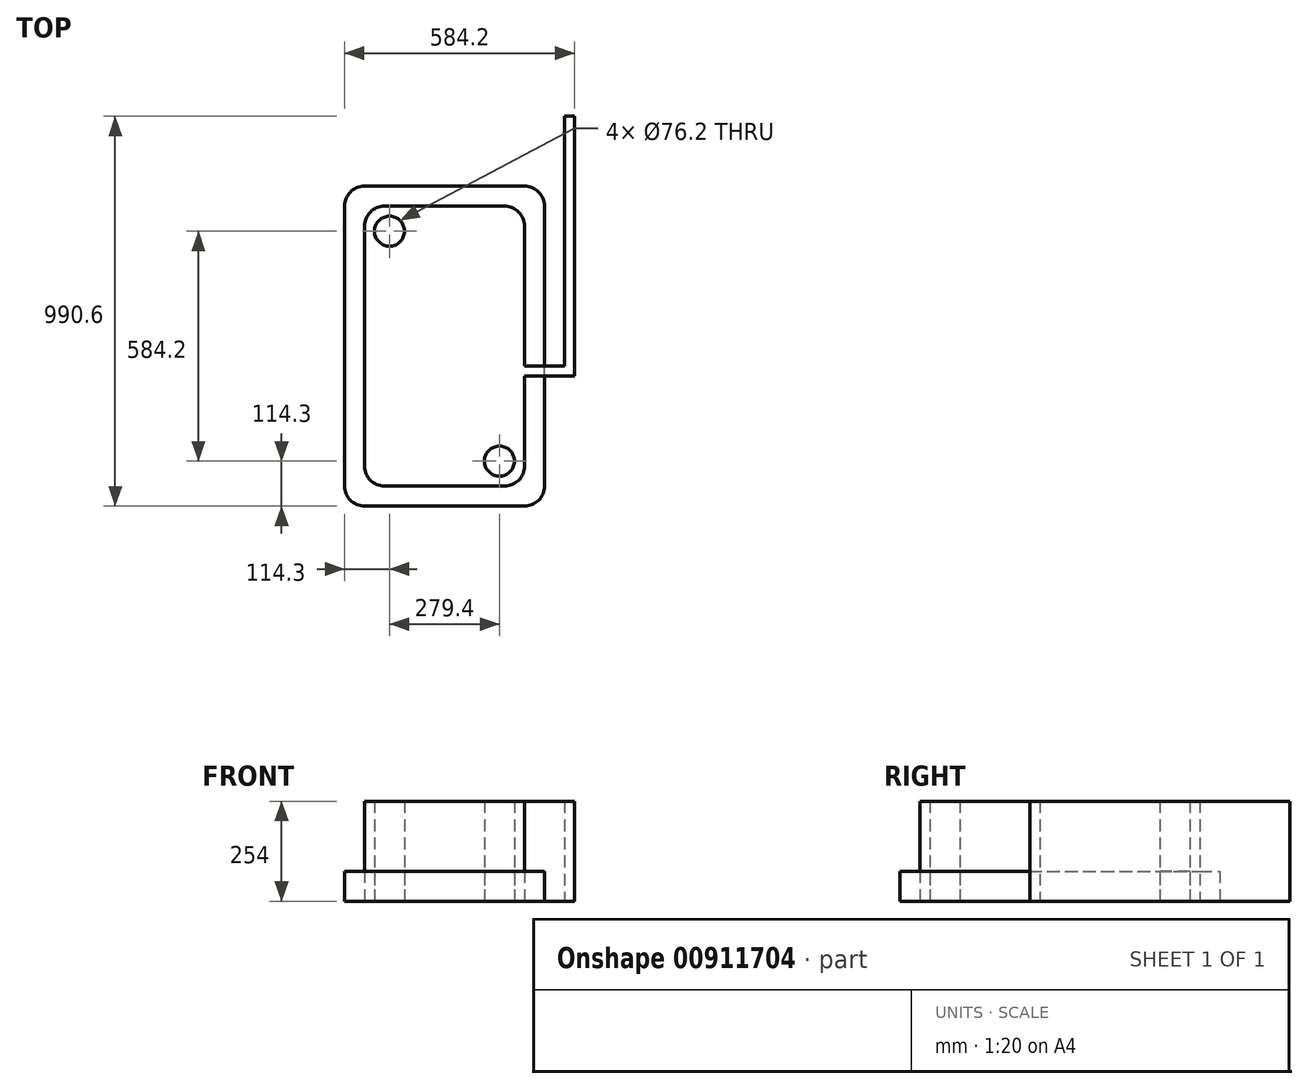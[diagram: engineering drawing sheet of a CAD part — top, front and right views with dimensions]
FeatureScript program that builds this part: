
annotation { "Feature Type Name" : "Feature", "Feature Type Description" : "" }
export const myFeature = defineFeature(function(context is Context, id is Id, definition is map)
    precondition{}
    {
        {
            var Q0;
            Q0=qCreatedBy(makeId("Top.planeOp"),FACE);
            var sketch = newSketch(context, id + "F0", { "sketchPlane" : qUnion([Q0])});
            skLineSegment(sketch, "E0.bottom", {"start": v(-203.2, -355.6) * mm, "end": v(203.2, -355.6) * mm});
            skLineSegment(sketch, "E0.top", {"start": v(-203.2, 355.6) * mm, "end": v(203.2, 355.6) * mm});
            skLineSegment(sketch, "E0.left", {"start": v(-203.2, -355.6) * mm, "end": v(-203.2, 355.6) * mm});
            skLineSegment(sketch, "E0.right", {"start": v(203.2, -355.6) * mm, "end": v(203.2, 355.6) * mm});
            skPoint(sketch, "E0.middle", {"position": v(0, 0) * mm});
            skCircle(sketch, "E1", {"center": v(-139.7, 292.1) * mm, "radius": 38.1 * mm});
            skCircle(sketch, "E2", {"center": v(139.7, -292.1) * mm, "radius": 38.1 * mm});
            skPoint(sketch, "E3", {"position": v(203.2, -76.2) * mm});
            skLineSegment(sketch, "E4", {"start": v(330.2, -76.2) * mm, "end": v(330.2, 584.2) * mm});
            skLineSegment(sketch, "E5", {"start": v(203.2, -76.2) * mm, "end": v(330.2, -76.2) * mm});
            skLineSegment(sketch, "E6.0", {"start": v(304.8, -50.8) * mm, "end": v(304.8, 584.2) * mm});
            skLineSegment(sketch, "E6.1", {"start": v(203.2, -50.8) * mm, "end": v(304.8, -50.8) * mm});
            skLineSegment(sketch, "E7", {"start": v(304.8, 584.2) * mm, "end": v(330.2, 584.2) * mm});
            skSolve(sketch);
        }
        {
            var Q0;
            {var subQ1=sQuery(id+"F0.wireOp",EDGE,"E0.bottom");Q0=makeQuery(id+"F0.imprint","IMPRINT",FACE,{"disambiguationData":[TD([[makeQuery(id+"F0.imprint","IMPRINT",EDGE,{"derivedFrom":subQ1}),1.0]])]});}
            var Q1;
            Q1=makeQuery(id+"F0.imprint","IMPRINT",FACE,{"disambiguationData":[TD([[makeQuery(id+"F0.imprint","IMPRINT",EDGE,{"derivedFrom":sQuery(id+"F0.wireOp",EDGE,"E4")}),1.0]])]});
            extrude(context, id + "F1", {"entities" : qUnion([Q0, Q1]), "depth" : 254 * mm, "offsetDistance" : 25.4 * mm});
        }
        {
            var Q0;
            Q0=makeQuery(id+"F1.opExtrude","SWEPT_EDGE",EDGE,{"disambiguationData":[OSD([sQuery(id+"F0.wireOp",EDGE,"E0.top"),sQuery(id+"F0.wireOp",EDGE,"E0.left")])]});
            var Q1;
            Q1=makeQuery(id+"F1.opExtrude","SWEPT_EDGE",EDGE,{"disambiguationData":[OSD([sQuery(id+"F0.wireOp",EDGE,"E0.top"),sQuery(id+"F0.wireOp",EDGE,"E0.right")])]});
            var Q2;
            Q2=makeQuery(id+"F1.opExtrude","SWEPT_EDGE",EDGE,{"disambiguationData":[OSD([sQuery(id+"F0.wireOp",EDGE,"E0.bottom"),sQuery(id+"F0.wireOp",EDGE,"E0.left")])]});
            var Q3;
            Q3=makeQuery(id+"F1.opExtrude","SWEPT_EDGE",EDGE,{"disambiguationData":[OSD([sQuery(id+"F0.wireOp",EDGE,"E0.bottom"),sQuery(id+"F0.wireOp",EDGE,"E0.right")])]});
            fillet(context, id + "F2", {"entities" : qUnion([Q0, Q1, Q2, Q3]), "radius" : 50.8 * mm, "tangentPropagation" : true, "allowEdgeOverflow" : false});
        }
        {
            var Q0;
            Q0=qCreatedBy(makeId("Top.planeOp"),FACE);
            var sketch = newSketch(context, id + "F3", { "sketchPlane" : qUnion([Q0])});
            skLineSegment(sketch, "E8.bottom", {"start": v(-254, -406.4) * mm, "end": v(254, -406.4) * mm});
            skLineSegment(sketch, "E8.top", {"start": v(-254, 406.4) * mm, "end": v(254, 406.4) * mm});
            skLineSegment(sketch, "E8.left", {"start": v(-254, -406.4) * mm, "end": v(-254, 406.4) * mm});
            skLineSegment(sketch, "E8.right", {"start": v(254, -406.4) * mm, "end": v(254, 406.4) * mm});
            skPoint(sketch, "E8.middle", {"position": v(0, 0) * mm});
            skCircle(sketch, "E9", {"center": v(-139.7, 292.1) * mm, "radius": 38.1 * mm});
            skCircle(sketch, "E10", {"center": v(139.7, -292.1) * mm, "radius": 38.1 * mm});
            skSolve(sketch);
        }
        {
            var Q0;
            Q0 = qSketchRegion(id + "F3", true);
            extrude(context, id + "F4", {"entities" : qUnion([Q0]), "depth" : 76.2 * mm, "offsetDistance" : 25.4 * mm});
        }
        {
            var Q0;
            Q0=makeQuery(id+"F4.opExtrude","SWEPT_EDGE",EDGE,{"disambiguationData":[OSD([sQuery(id+"F3.wireOp",EDGE,"E8.bottom"),sQuery(id+"F3.wireOp",EDGE,"E8.right")])]});
            var Q1;
            Q1=makeQuery(id+"F4.opExtrude","SWEPT_EDGE",EDGE,{"disambiguationData":[OSD([sQuery(id+"F3.wireOp",EDGE,"E8.bottom"),sQuery(id+"F3.wireOp",EDGE,"E8.left")])]});
            var Q2;
            Q2=makeQuery(id+"F4.opExtrude","SWEPT_EDGE",EDGE,{"disambiguationData":[OSD([sQuery(id+"F3.wireOp",EDGE,"E8.top"),sQuery(id+"F3.wireOp",EDGE,"E8.left")])]});
            var Q3;
            Q3=makeQuery(id+"F4.opExtrude","SWEPT_EDGE",EDGE,{"disambiguationData":[OSD([sQuery(id+"F3.wireOp",EDGE,"E8.top"),sQuery(id+"F3.wireOp",EDGE,"E8.right")])]});
            fillet(context, id + "F5", {"entities" : qUnion([Q0, Q1, Q2, Q3]), "radius" : 50.8 * mm, "tangentPropagation" : true, "allowEdgeOverflow" : false});
        }
    });
